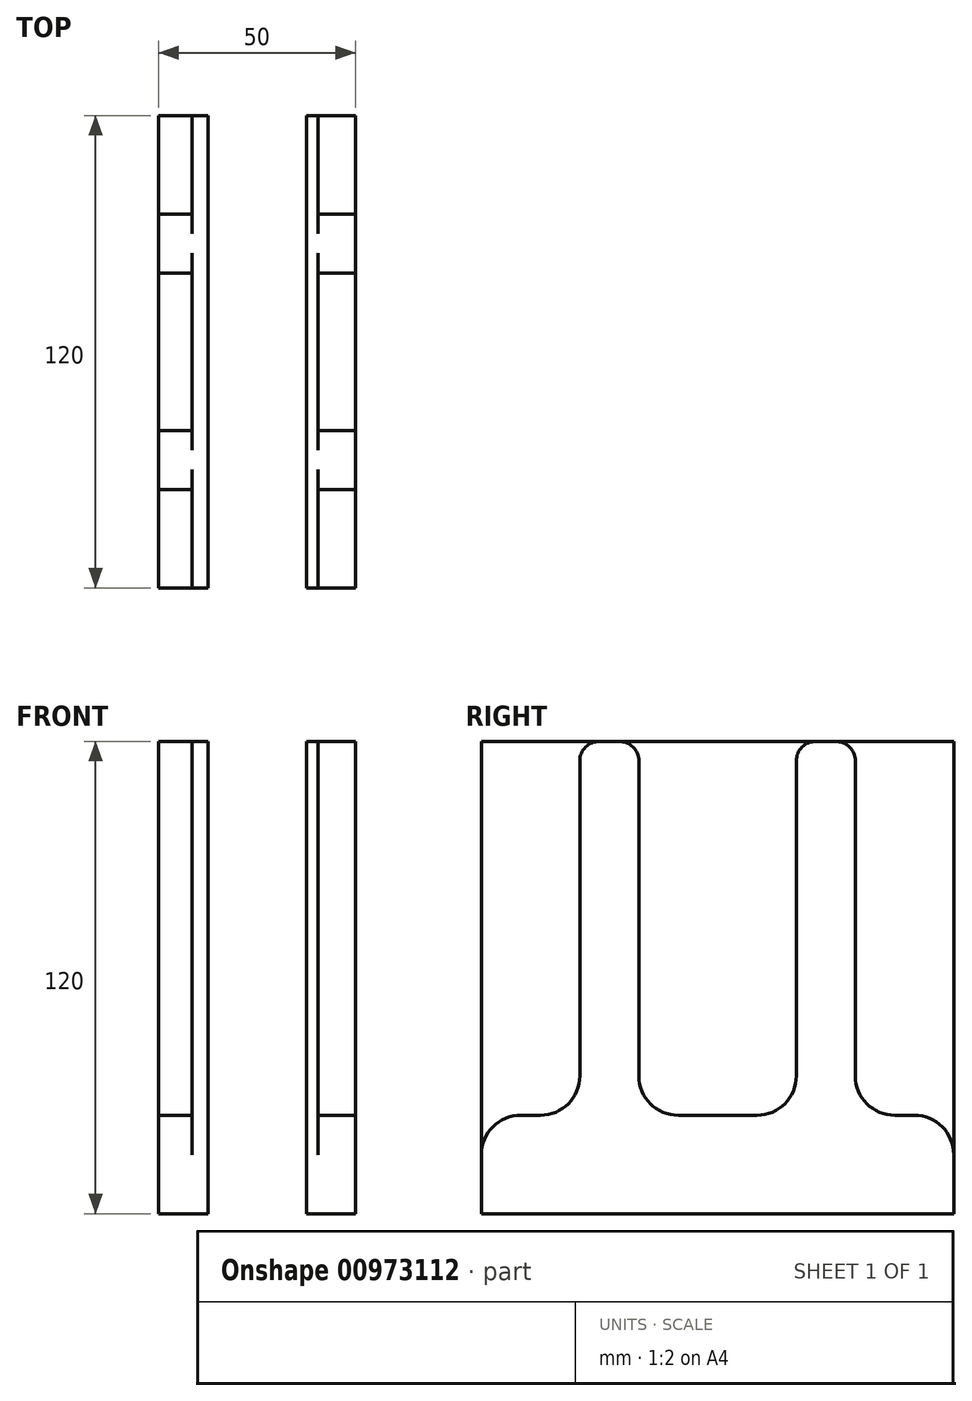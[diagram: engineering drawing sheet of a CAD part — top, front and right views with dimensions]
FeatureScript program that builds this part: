
annotation { "Feature Type Name" : "Feature", "Feature Type Description" : "" }
export const myFeature = defineFeature(function(context is Context, id is Id, definition is map)
    precondition{}
    {
        {
            var Q0;
            Q0=qCreatedBy(makeId("Right.planeOp"),FACE);
            var sketch = newSketch(context, id + "F0", { "sketchPlane" : qUnion([Q0])});
            skLineSegment(sketch, "E0.bottom", {"start": v(-37.49, -12.55) * mm, "end": v(-32.49, -12.55) * mm});
            skLineSegment(sketch, "E0.top", {"start": v(-47.49, -37.55) * mm, "end": v(72.51, -37.55) * mm});
            skLineSegment(sketch, "E0.left", {"start": v(-47.49, -22.55) * mm, "end": v(-47.49, -37.55) * mm});
            skLineSegment(sketch, "E0.right", {"start": v(72.51, -22.55) * mm, "end": v(72.51, -37.55) * mm});
            skLineSegment(sketch, "E1.top", {"start": v(-17.49, 82.45) * mm, "end": v(-12.49, 82.45) * mm});
            skLineSegment(sketch, "E1.left", {"start": v(-22.49, -2.55) * mm, "end": v(-22.49, 77.45) * mm});
            skLineSegment(sketch, "E1.right", {"start": v(-7.49, -2.55) * mm, "end": v(-7.49, 77.45) * mm});
            skLineSegment(sketch, "E2.top", {"start": v(37.51, 82.45) * mm, "end": v(42.51, 82.45) * mm});
            skLineSegment(sketch, "E2.left", {"start": v(32.51, -2.55) * mm, "end": v(32.51, 77.45) * mm});
            skLineSegment(sketch, "E2.right", {"start": v(47.51, -2.55) * mm, "end": v(47.51, 77.45) * mm});
            skLineSegment(sketch, "E3.trimOffspring", {"start": v(57.51, -12.55) * mm, "end": v(62.51, -12.55) * mm});
            skLineSegment(sketch, "E4.trimOffspring", {"start": v(2.51, -12.55) * mm, "end": v(22.51, -12.55) * mm});
            skPoint(sketch, "E5.visualSharp", {"position": v(47.51, 82.45) * mm});
            skArc(sketch, "E5.filletArc", {"start": v(47.51, 77.45) * mm, "mid": v(46.05, 80.98) * mm, "end": v(42.51, 82.45) * mm});
            skPoint(sketch, "E6.visualSharp", {"position": v(32.51, 82.45) * mm});
            skArc(sketch, "E6.filletArc", {"start": v(37.51, 82.45) * mm, "mid": v(33.98, 80.98) * mm, "end": v(32.51, 77.45) * mm});
            skPoint(sketch, "E7.visualSharp", {"position": v(-7.49, 82.45) * mm});
            skArc(sketch, "E7.filletArc", {"start": v(-7.49, 77.45) * mm, "mid": v(-8.95, 80.98) * mm, "end": v(-12.49, 82.45) * mm});
            skPoint(sketch, "E8.visualSharp", {"position": v(-22.49, 82.45) * mm});
            skArc(sketch, "E8.filletArc", {"start": v(-17.49, 82.45) * mm, "mid": v(-21.02, 80.98) * mm, "end": v(-22.49, 77.45) * mm});
            skPoint(sketch, "E9.visualSharp", {"position": v(-7.49, -12.55) * mm});
            skArc(sketch, "E9.filletArc", {"start": v(-7.49, -2.55) * mm, "mid": v(-4.56, -9.62) * mm, "end": v(2.51, -12.55) * mm});
            skPoint(sketch, "E10.visualSharp", {"position": v(32.51, -12.55) * mm});
            skArc(sketch, "E10.filletArc", {"start": v(22.51, -12.55) * mm, "mid": v(29.58, -9.62) * mm, "end": v(32.51, -2.55) * mm});
            skPoint(sketch, "E11.visualSharp", {"position": v(-22.49, -12.55) * mm});
            skArc(sketch, "E11.filletArc", {"start": v(-32.49, -12.55) * mm, "mid": v(-25.42, -9.62) * mm, "end": v(-22.49, -2.55) * mm});
            skPoint(sketch, "E12.visualSharp", {"position": v(47.51, -12.55) * mm});
            skArc(sketch, "E12.filletArc", {"start": v(47.51, -2.55) * mm, "mid": v(50.44, -9.62) * mm, "end": v(57.51, -12.55) * mm});
            skPoint(sketch, "E13.visualSharp", {"position": v(72.51, -12.55) * mm});
            skArc(sketch, "E13.filletArc", {"start": v(72.51, -22.55) * mm, "mid": v(69.58, -15.48) * mm, "end": v(62.51, -12.55) * mm});
            skPoint(sketch, "E14.visualSharp", {"position": v(-47.49, -12.55) * mm});
            skArc(sketch, "E14.filletArc", {"start": v(-37.49, -12.55) * mm, "mid": v(-44.56, -15.48) * mm, "end": v(-47.49, -22.55) * mm});
            skSolve(sketch);
        }
        {
            var Q0;
            Q0=makeQuery(id+"F0.imprint","IMPRINT",FACE,{"disambiguationData":[TD([[makeQuery(id+"F0.imprint","IMPRINT",EDGE,{"derivedFrom":sQuery(id+"F0.wireOp",EDGE,"E0.bottom")}),-1.0]])]});
            extrude(context, id + "F1", {"entities" : qUnion([Q0]), "depth" : 50 * mm, "offsetDistance" : 25 * mm});
        }
        {
            var Q0;
            Q0=makeQuery(id+"F1.opExtrude","SWEPT_FACE",FACE,{"disambiguationData":[OSD([sQuery(id+"F0.wireOp",EDGE,"E0.right")])]});
            var sketch = newSketch(context, id + "F2", { "sketchPlane" : qUnion([Q0])});
            skLineSegment(sketch, "E15.bottom", {"start": v(-40.52, -37.55) * mm, "end": v(-8.52, -37.55) * mm});
            skLineSegment(sketch, "E15.top", {"start": v(-40.52, 82.45) * mm, "end": v(-8.52, 82.45) * mm});
            skLineSegment(sketch, "E15.left", {"start": v(-40.52, -37.55) * mm, "end": v(-40.52, 82.45) * mm});
            skLineSegment(sketch, "E15.right", {"start": v(-8.52, -37.55) * mm, "end": v(-8.52, 82.45) * mm});
            skSolve(sketch);
        }
        {
            var Q0;
            {var subQ0=sQuery(id+"F2.wireOp",EDGE,"E15.top");Q0=makeQuery(id+"F2.imprint","IMPRINT",FACE,{"disambiguationData":[TD([[makeQuery(id+"F2.imprint","IMPRINT",EDGE,{"derivedFrom":subQ0}),-1.0]])]});}
            extrude(context, id + "F3", {"entities" : qUnion([Q0]), "operationType" : NewBodyOperationType.ADD, "oppositeDirection" : true, "depth" : 120 * mm, "offsetDistance" : 25 * mm});
        }
        {
            var Q0;
            {var subQ0=sQuery(id+"F0.wireOp",EDGE,"E0.right");Q0=makeQuery(id+"F3.boolean.opBoolean","MERGE",FACE,{"derivedFrom":[makeQuery(id+"F1.opExtrude","SWEPT_FACE",FACE,{"disambiguationData":[OSD([subQ0])]}),makeQuery(id+"F3.opExtrude","CAP_FACE",FACE,{"disambiguationData":[OSD([subQ0,sQuery(id+"F0.wireOp",EDGE,"E13.filletArc"),sQuery(id+"F2.wireOp",EDGE,"E15.top"),sQuery(id+"F2.wireOp",EDGE,"E15.left"),sQuery(id+"F2.wireOp",EDGE,"E15.right")])],"isStart":true})]});}
            var sketch = newSketch(context, id + "F4", { "sketchPlane" : qUnion([Q0])});
            skLineSegment(sketch, "E16.bottom", {"start": v(-37.52, 82.45) * mm, "end": v(-12.52, 82.45) * mm});
            skLineSegment(sketch, "E16.top", {"start": v(-37.52, -37.55) * mm, "end": v(-12.52, -37.55) * mm});
            skLineSegment(sketch, "E16.left", {"start": v(-37.52, 82.45) * mm, "end": v(-37.52, -37.55) * mm});
            skLineSegment(sketch, "E16.right", {"start": v(-12.52, 82.45) * mm, "end": v(-12.52, -37.55) * mm});
            skSolve(sketch);
        }
        {
            var Q0;
            Q0=makeQuery(id+"F4.imprint","IMPRINT",FACE,{"disambiguationData":[TD([[makeQuery(id+"F4.imprint","IMPRINT",EDGE,{"derivedFrom":sQuery(id+"F4.wireOp",EDGE,"E16.bottom")}),-1.0]])]});
            extrude(context, id + "F5", {"entities" : qUnion([Q0]), "operationType" : NewBodyOperationType.REMOVE, "endBound" : BoundingType.THROUGH_ALL, "oppositeDirection" : true, "depth" : 25 * mm, "offsetDistance" : 25 * mm});
        }
    });
